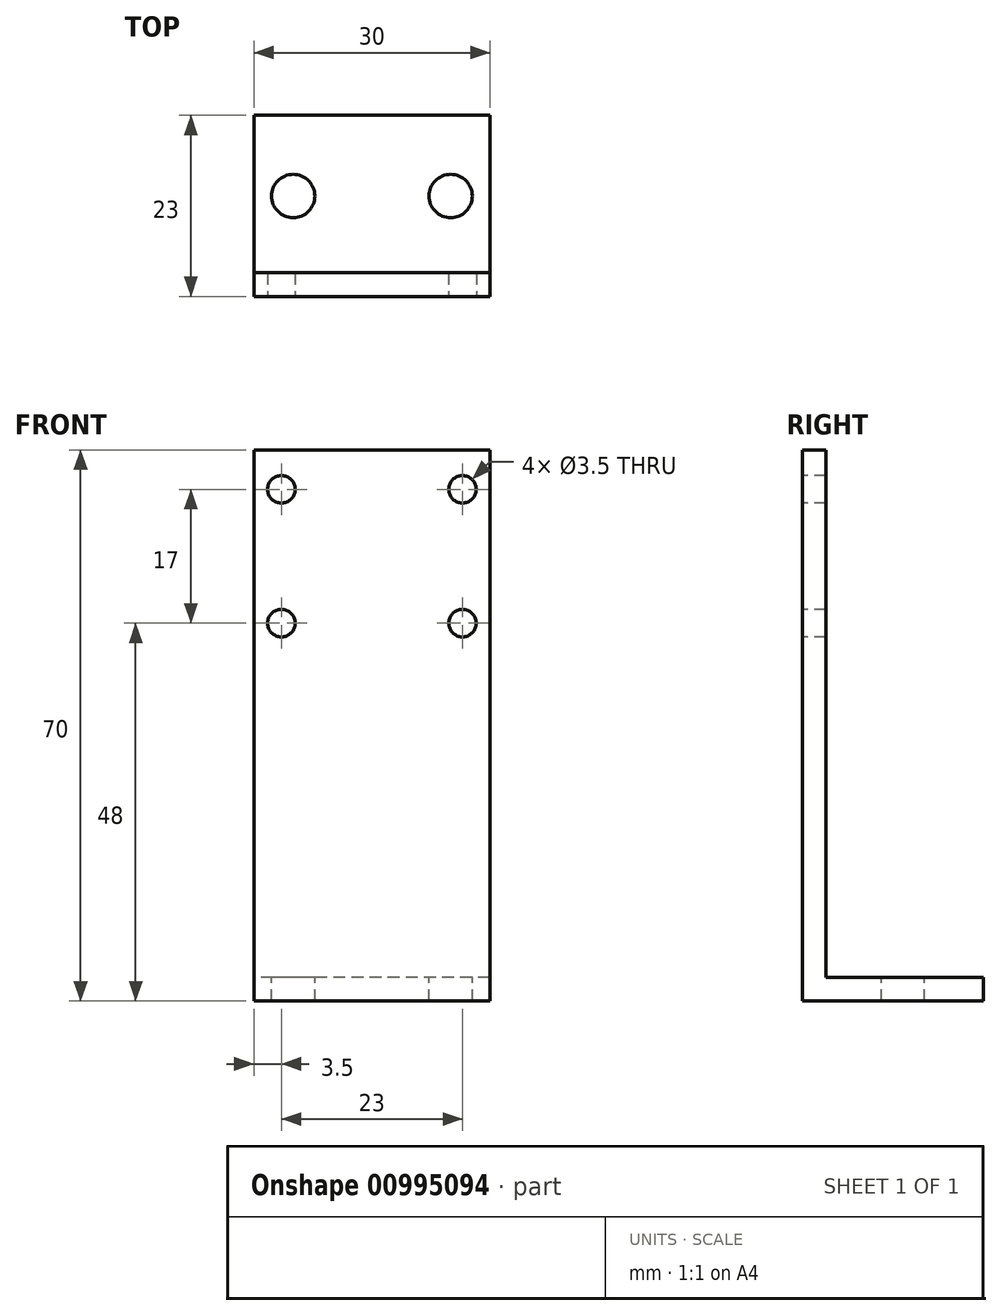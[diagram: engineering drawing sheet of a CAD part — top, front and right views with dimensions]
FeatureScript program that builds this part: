
annotation { "Feature Type Name" : "Feature", "Feature Type Description" : "" }
export const myFeature = defineFeature(function(context is Context, id is Id, definition is map)
    precondition{}
    {
        {
            var Q0;
            Q0=qCreatedBy(makeId("Front.planeOp"),FACE);
            var sketch = newSketch(context, id + "F0", { "sketchPlane" : qUnion([Q0])});
            skLineSegment(sketch, "E0.bottom", {"start": v(-12.5, 70) * mm, "end": v(17.5, 70) * mm});
            skLineSegment(sketch, "E0.top", {"start": v(-12.5, 0) * mm, "end": v(17.5, 0) * mm});
            skLineSegment(sketch, "E0.left", {"start": v(-12.5, 70) * mm, "end": v(-12.5, 0) * mm});
            skLineSegment(sketch, "E0.right", {"start": v(17.5, 70) * mm, "end": v(17.5, 0) * mm});
            skSolve(sketch);
        }
        {
            var Q0;
            Q0=qSketchRegion(id+"F0",true);
            extrude(context, id + "F1", {"entities" : qUnion([Q0]), "depth" : 3 * mm, "offsetDistance" : 25 * mm});
        }
        {
            var Q0;
            Q0=makeQuery(id+"F1.opExtrude","CAP_FACE",FACE,{"disambiguationData":[OSD([sQuery(id+"F0.wireOp",EDGE,"E0.bottom"),sQuery(id+"F0.wireOp",EDGE,"E0.top"),sQuery(id+"F0.wireOp",EDGE,"E0.left"),sQuery(id+"F0.wireOp",EDGE,"E0.right")])],"isStart":true});
            var sketch = newSketch(context, id + "F2", { "sketchPlane" : qUnion([Q0])});
            skLineSegment(sketch, "E1.bottom", {"start": v(-17.5, 0) * mm, "end": v(12.5, 0) * mm});
            skLineSegment(sketch, "E1.top", {"start": v(-17.5, 3) * mm, "end": v(12.5, 3) * mm});
            skLineSegment(sketch, "E1.left", {"start": v(-17.5, 0) * mm, "end": v(-17.5, 3) * mm});
            skLineSegment(sketch, "E1.right", {"start": v(12.5, 0) * mm, "end": v(12.5, 3) * mm});
            skSolve(sketch);
        }
        {
            var Q0;
            Q0=qSketchRegion(id+"F2",true);
            extrude(context, id + "F3", {"entities" : qUnion([Q0]), "operationType" : NewBodyOperationType.ADD, "depth" : 20 * mm, "offsetDistance" : 25 * mm});
        }
        {
            var Q0;
            Q0=makeQuery(id+"F3.opExtrude","SWEPT_FACE",FACE,{"disambiguationData":[OSD([sQuery(id+"F2.wireOp",EDGE,"E1.top")])]});
            var sketch = newSketch(context, id + "F4", { "sketchPlane" : qUnion([Q0])});
            skCircle(sketch, "E2", {"center": v(12.5, 9.76) * mm, "radius": 2.75 * mm});
            skCircle(sketch, "E3", {"center": v(-7.5, 9.76) * mm, "radius": 2.75 * mm});
            skSolve(sketch);
        }
        {
            var Q0;
            Q0=qSketchRegion(id+"F4",true);
            extrude(context, id + "F5", {"entities" : qUnion([Q0]), "operationType" : NewBodyOperationType.REMOVE, "endBound" : BoundingType.THROUGH_ALL, "oppositeDirection" : true, "depth" : 25 * mm, "offsetDistance" : 25 * mm});
        }
        {
            var Q0;
            Q0=makeQuery(id+"F1.opExtrude","CAP_FACE",FACE,{"disambiguationData":[OSD([sQuery(id+"F0.wireOp",EDGE,"E0.bottom"),sQuery(id+"F0.wireOp",EDGE,"E0.top"),sQuery(id+"F0.wireOp",EDGE,"E0.left"),sQuery(id+"F0.wireOp",EDGE,"E0.right")])],"isStart":false});
            var sketch = newSketch(context, id + "F6", { "sketchPlane" : qUnion([Q0])});
            skCircle(sketch, "E4", {"center": v(-9, 65) * mm, "radius": 1.75 * mm});
            skCircle(sketch, "E5", {"center": v(-9, 48) * mm, "radius": 1.75 * mm});
            skLineSegment(sketch, "E6", {"start": v(2.5, 70) * mm, "end": v(2.5, 38.23) * mm});
            skCircle(sketch, "E7.MirrorC", {"center": v(14, 65) * mm, "radius": 1.75 * mm});
            skCircle(sketch, "E8.MirrorC", {"center": v(14, 48) * mm, "radius": 1.75 * mm});
            skSolve(sketch);
        }
        {
            var Q0;
            Q0=qSketchRegion(id+"F6",true);
            extrude(context, id + "F7", {"entities" : qUnion([Q0]), "operationType" : NewBodyOperationType.REMOVE, "endBound" : BoundingType.THROUGH_ALL, "oppositeDirection" : true, "depth" : 25 * mm, "offsetDistance" : 25 * mm});
        }
    });
